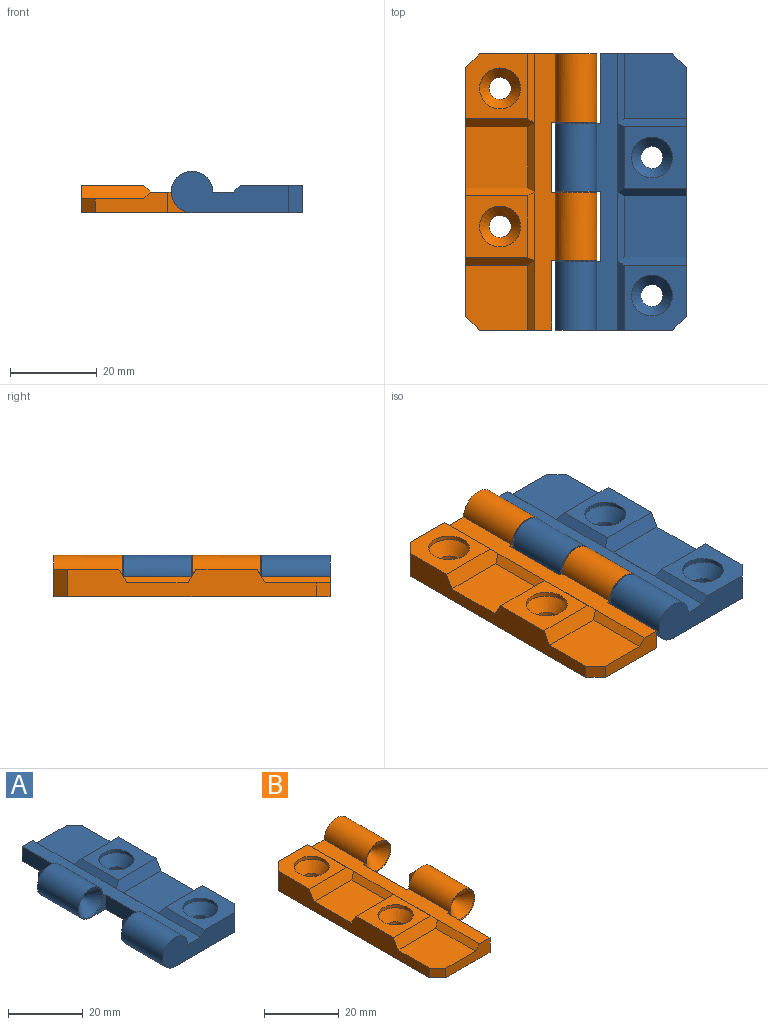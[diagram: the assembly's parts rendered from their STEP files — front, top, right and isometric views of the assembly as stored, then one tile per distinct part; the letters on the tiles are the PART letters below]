
ASSEMBLY  parts=2 mates=1
PART A: 40 faces, bbox 30.9x63.5x10.9 mm
  f0: plane 63.5x4.76mm, normal (0,0,1), area 276.7mm2, adj f1,f2,f3,f4,f5,f6,f7,f9
  f1: plane 16.67x4.76mm, normal (0,1,0), area 60.5mm2, adj f0,f9,f11,f27,f30,f38
  f2: plane 5.56x4.76mm, normal (0,1,0), area 8.6mm2, adj f0,f9,f11,f19
  f3: plane 5.56x4.76mm, normal (0,1,0), area 8.6mm2, adj f0,f10,f11,f16
  f4: cylinder r=4.76mm len=15.68mm, axis (0,-1,0), area 351.8mm2, adj f0,f5,f11,f16
  f5: plane 26.99x9.53mm, normal (0,-1,0), area 178.2mm2, adj f0,f4,f11,f22,f29,f39
  f6: cylinder r=4.76mm len=15.48mm, axis (0,-1,0), area 347.4mm2, adj f0,f11,f12,f19
  f7: plane 5.56x4.76mm, normal (0,-1,0), area 8.6mm2, adj f0,f10,f11,f12
  f8: plane 57.15x6.35mm, normal (1,0,0), area 272.2mm2, adj f11,f21,f22,f23,f24,f25,f26,f27
  f9: plane 16.07x4.76mm, normal (-1,0,0), area 76.5mm2, adj f0,f1,f2,f11
  f10: plane 16.27x4.76mm, normal (-1,0,0), area 77.5mm2, adj f0,f3,f7,f11
  f11: plane 63.5x25.4mm, normal (0,0,-1), area 1382.6mm2, adj f1,f2,f3,f4,f5,f6,f7,f8
  f12: torus R=4.76mm, axis (0,1,0), area 9mm2, adj f6,f7,f14
  f13: sphere r=1.19mm, area 2.6mm2, adj f14
  f14: cone r=4.48mm half-angle=45deg, axis (0,-1,0), area 86.1mm2, adj f12,f13
  f15: cone r=4.2mm half-angle=45deg, axis (0,-1,0), area 77mm2, adj f16,f17
  f16: torus R=4.76mm, axis (0,-1,0), area 17.5mm2, adj f3,f4,f15
  f17: sphere r=0.79mm, area 1.2mm2, adj f15
  f18: cone r=4.2mm half-angle=45deg, axis (0,-1,0), area 77mm2, adj f19,f20
  f19: torus R=4.76mm, axis (0,-1,0), area 17.5mm2, adj f2,f6,f18
  f20: sphere r=0.79mm, area 1.2mm2, adj f18
  f21: plane 15.88x3.18mm, normal (0,0.87,0.5), area 55.3mm2, adj f8,f22,f26,f29,f31
  f22: plane 14.96x14.29mm, normal (0,0,1), area 139.3mm2, adj f5,f8,f21,f29,f34,f39
  f23: plane 15.88x3.18mm, normal (0,-0.87,0.5), area 55.3mm2, adj f8,f25,f26,f28,f31
  f24: plane 15.88x3.18mm, normal (0,0.87,0.5), area 55.3mm2, adj f8,f25,f27,f28,f30
  f25: plane 14.29x14.04mm, normal (0,0,1), area 131.3mm2, adj f8,f23,f24,f28,f37
  f26: plane 14.29x14.04mm, normal (0,0,1), area 200.6mm2, adj f8,f21,f23,f31
  f27: plane 14.96x14.29mm, normal (0,0,1), area 208.7mm2, adj f1,f8,f24,f30,f38
  f28: plane 15.88x1.59mm, normal (-0.71,0,0.71), area 33.6mm2, adj f0,f23,f24,f25
  f29: plane 15.88x1.59mm, normal (-0.71,0,0.71), area 34.6mm2, adj f0,f5,f21,f22
  f30: plane 15.88x1.59mm, normal (0.71,0,0.71), area 34.6mm2, adj f0,f1,f24,f27
  f31: plane 15.88x1.59mm, normal (0.71,0,0.71), area 33.6mm2, adj f0,f21,f23,f26
  f32: cylinder r=2.54mm len=5.08mm, axis (0,0,-1), area 35.9mm2, adj f11,f33
  f33: cone r=4.7mm half-angle=35deg, axis (0,0,1), area 85.6mm2, adj f32,f34
  f34: cylinder r=4.7mm len=9.4mm, axis (0,0,-1), area 30mm2, adj f22,f33
  f35: cylinder r=2.54mm len=5.08mm, axis (0,0,-1), area 35.9mm2, adj f11,f36
  f36: cone r=4.7mm half-angle=35deg, axis (0,0,1), area 85.6mm2, adj f35,f37
  f37: cylinder r=4.7mm len=9.4mm, axis (0,0,-1), area 30mm2, adj f25,f36
  f38: plane 3.18x3.18mm, normal (0.71,0.71,0), area 14.3mm2, adj f1,f8,f11,f27
  f39: plane 6.35x3.18mm, normal (0.71,-0.71,0), area 28.5mm2, adj f5,f8,f11,f22
PART B: 40 faces, bbox 30.9x63.5x10.9 mm
  f0: plane 57.15x6.35mm, normal (-1,0,0), area 272.2mm2, adj f10,f21,f22,f23,f24,f25,f26,f27
  f1: cylinder r=4.76mm len=15.68mm, axis (0,-1,0), area 351.8mm2, adj f2,f10,f11,f15
  f2: plane 26.99x9.53mm, normal (0,1,0), area 178.2mm2, adj f1,f10,f11,f22,f29,f38
  f3: plane 5.56x4.76mm, normal (0,-1,0), area 8.6mm2, adj f9,f10,f11,f15
  f4: cylinder r=4.76mm len=15.48mm, axis (0,-1,0), area 347.4mm2, adj f10,f11,f14,f19
  f5: plane 5.56x4.76mm, normal (0,1,0), area 8.6mm2, adj f9,f10,f11,f19
  f6: plane 5.56x4.76mm, normal (0,-1,0), area 8.6mm2, adj f8,f10,f11,f14
  f7: plane 16.67x4.76mm, normal (0,-1,0), area 60.5mm2, adj f8,f10,f11,f27,f30,f39
  f8: plane 16.07x4.76mm, normal (1,0,0), area 76.5mm2, adj f6,f7,f10,f11
  f9: plane 16.27x4.76mm, normal (1,0,0), area 77.5mm2, adj f3,f5,f10,f11
  f10: plane 63.5x25.4mm, normal (0,0,-1), area 1382.6mm2, adj f0,f1,f2,f3,f4,f5,f6,f7
  f11: plane 63.5x4.76mm, normal (0,0,1), area 276.7mm2, adj f1,f2,f3,f4,f5,f6,f7,f8
  f12: sphere r=1.19mm, area 2.6mm2, adj f13
  f13: cone r=4.48mm half-angle=45deg, axis (0,-1,0), area 86.1mm2, adj f12,f14
  f14: torus R=4.76mm, axis (0,1,0), area 9mm2, adj f4,f6,f13
  f15: torus R=4.76mm, axis (0,1,0), area 9mm2, adj f1,f3,f17
  f16: sphere r=1.19mm, area 2.6mm2, adj f17
  f17: cone r=4.48mm half-angle=45deg, axis (0,-1,0), area 86.1mm2, adj f15,f16
  f18: cone r=4.2mm half-angle=45deg, axis (0,-1,0), area 77mm2, adj f19,f20
  f19: torus R=4.76mm, axis (0,-1,0), area 17.5mm2, adj f4,f5,f18
  f20: sphere r=0.79mm, area 1.2mm2, adj f18
  f21: plane 15.88x3.18mm, normal (0,-0.87,0.5), area 55.3mm2, adj f0,f22,f26,f29,f31
  f22: plane 14.96x14.29mm, normal (0,0,1), area 139.3mm2, adj f0,f2,f21,f29,f32,f38
  f23: plane 15.88x3.18mm, normal (0,0.87,0.5), area 55.3mm2, adj f0,f25,f26,f28,f31
  f24: plane 15.88x3.18mm, normal (0,-0.87,0.5), area 55.3mm2, adj f0,f25,f27,f28,f30
  f25: plane 14.29x14.04mm, normal (0,0,1), area 131.3mm2, adj f0,f23,f24,f28,f35
  f26: plane 14.29x14.04mm, normal (0,0,1), area 200.6mm2, adj f0,f21,f23,f31
  f27: plane 14.96x14.29mm, normal (0,0,1), area 208.7mm2, adj f0,f7,f24,f30,f39
  f28: plane 15.88x1.59mm, normal (0.71,0,0.71), area 33.6mm2, adj f11,f23,f24,f25
  f29: plane 15.88x1.59mm, normal (0.71,0,0.71), area 34.6mm2, adj f2,f11,f21,f22
  f30: plane 15.88x1.59mm, normal (-0.71,0,0.71), area 34.6mm2, adj f7,f11,f24,f27
  f31: plane 15.88x1.59mm, normal (-0.71,0,0.71), area 33.6mm2, adj f11,f21,f23,f26
  f32: cylinder r=4.7mm len=9.4mm, axis (0,0,1), area 30mm2, adj f22,f33
  f33: cone r=4.7mm half-angle=35deg, axis (0,0,1), area 85.6mm2, adj f32,f34
  f34: cylinder r=2.54mm len=5.08mm, axis (0,0,1), area 35.9mm2, adj f10,f33
  f35: cylinder r=4.7mm len=9.4mm, axis (0,0,1), area 30mm2, adj f25,f36
  f36: cone r=4.7mm half-angle=35deg, axis (0,0,1), area 85.6mm2, adj f35,f37
  f37: cylinder r=2.54mm len=5.08mm, axis (0,0,1), area 35.9mm2, adj f10,f36
  f38: plane 6.35x3.18mm, normal (-0.71,0.71,0), area 28.5mm2, adj f0,f2,f10,f22
  f39: plane 3.18x3.18mm, normal (-0.71,-0.71,0), area 14.3mm2, adj f0,f7,f10,f27
PLACE A t=(0,-31.95,4.76)mm
PLACE B t=(0,-31.95,4.76)mm
MATE revolute A.f4 <-> B.f1  axis (0,1,0) through (0,-16.27,4.76)mm
